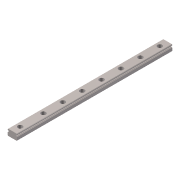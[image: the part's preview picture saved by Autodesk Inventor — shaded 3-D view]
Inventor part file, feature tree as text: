
AUTODESK INVENTOR PART (.ipt)
format: ipt  version: 2019.4 (Build 234330000, 330)  size: 210,432 bytes
history: mixed  units: mm
features: extrude x2, sketch x2, projected_geometry x2, other x1, pattern_linear x1, imported_body x1
ambient origin geometry x8: Origin, YZ Plane, XZ Plane, XY Plane, X Axis, Y Axis, Z Axis, Center Point
bodies: Solid1 (imported_parasolid)
feature tree (9):
  other  "Fill Pattern1"
  extrude  "Extrusion1"  Depth=25.0mm
  extrude  "Extrusion2"  Depth=210.0mm
  pattern_linear  "Rectangular Pattern1"  [2 undecoded]
  sketch  "Sketch1"  dims[d0=50.0mm d1=0.0mm d2=25.0mm]
  projected_geometry  "Projected Loop1"
  sketch  "Sketch2"  dims[d3=50.0mm d4=0.0mm d5=210.0mm d7=25.0mm]
  projected_geometry  "Projected Loop2"
  imported_body  NMx_Import_Brep_tag  [imported B-rep: ~35 faces, bbox_mm=[11.964657, 8.0, 200.0]]
note: 2 required parameter values undecoded (feature->parameter linkage not recoverable at this tier; creation-order binding heuristic only, values carry confidence <= 0.55)
